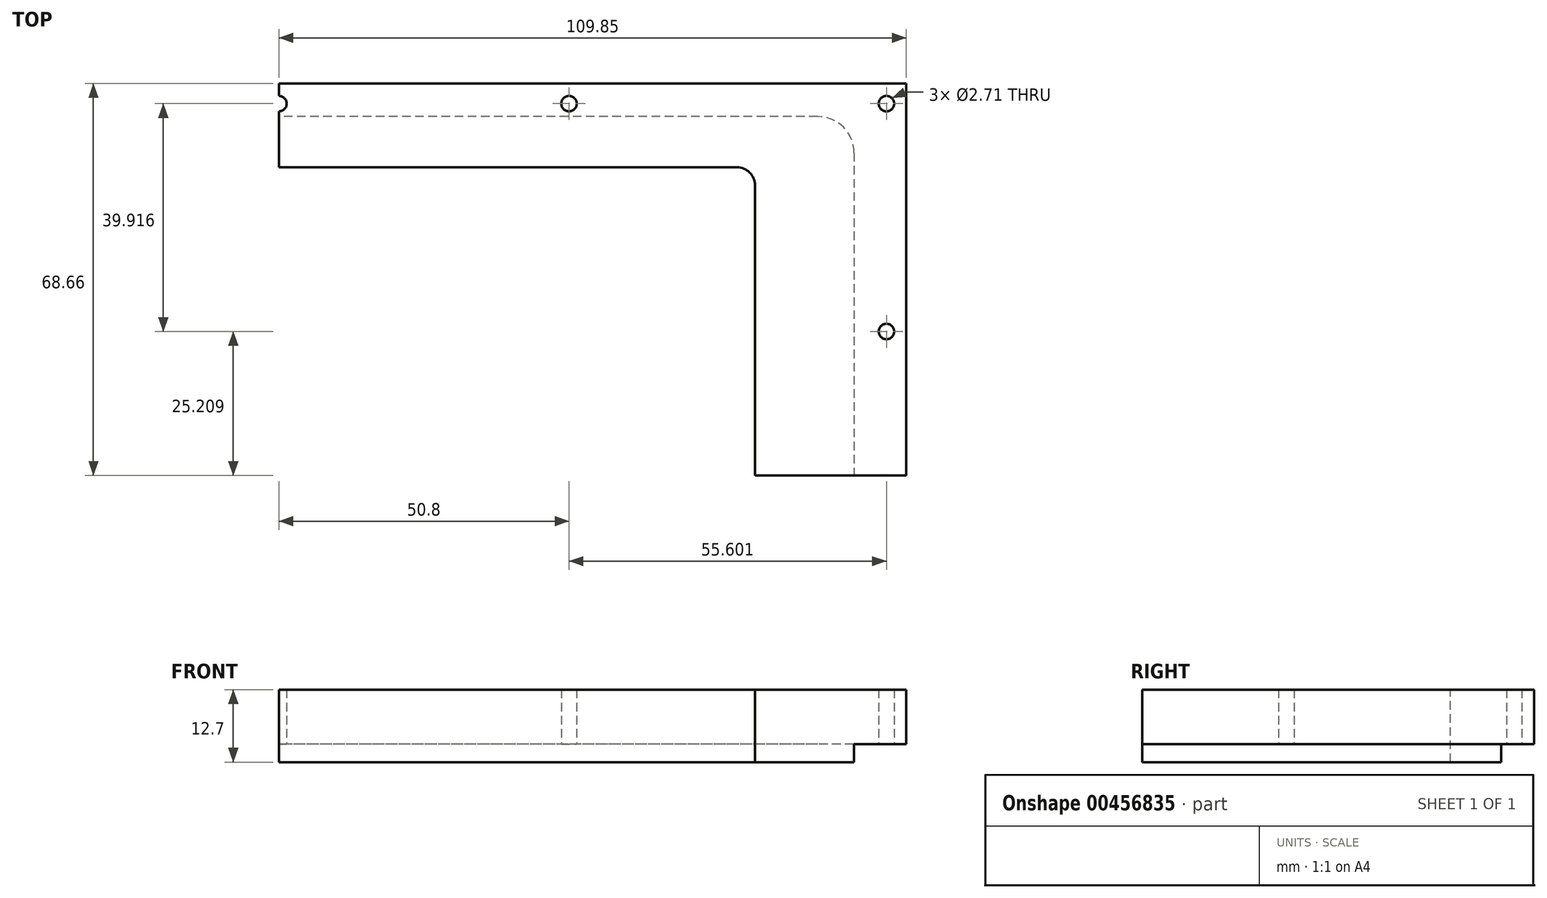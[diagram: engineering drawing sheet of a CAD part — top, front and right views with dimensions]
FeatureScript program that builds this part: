
annotation { "Feature Type Name" : "Feature", "Feature Type Description" : "" }
export const myFeature = defineFeature(function(context is Context, id is Id, definition is map)
    precondition{}
    {
        {
            var Q0;
            Q0=qCreatedBy(makeId("Top.planeOp"),FACE);
            var sketch = newSketch(context, id + "F0", { "sketchPlane" : qUnion([Q0])});
            skLineSegment(sketch, "E0.bottom", {"start": v(94.37, 62.86) * mm, "end": v(-94.37, 62.86) * mm});
            skLineSegment(sketch, "E0.top", {"start": v(94.37, -62.87) * mm, "end": v(-94.37, -62.87) * mm});
            skLineSegment(sketch, "E0.left", {"start": v(100.72, 56.51) * mm, "end": v(100.72, -56.52) * mm});
            skLineSegment(sketch, "E0.right", {"start": v(-100.72, 56.51) * mm, "end": v(-100.72, -56.52) * mm});
            skPoint(sketch, "E0.middle", {"position": v(0, 0) * mm});
            skPoint(sketch, "E1.visualSharp", {"position": v(-100.72, 62.86) * mm});
            skArc(sketch, "E1.filletArc", {"start": v(-94.37, 62.86) * mm, "mid": v(-98.86, 61) * mm, "end": v(-100.72, 56.51) * mm});
            skPoint(sketch, "E2.visualSharp", {"position": v(100.72, 62.86) * mm});
            skArc(sketch, "E2.filletArc", {"start": v(100.72, 56.51) * mm, "mid": v(98.86, 61) * mm, "end": v(94.37, 62.86) * mm});
            skPoint(sketch, "E3.visualSharp", {"position": v(100.72, -62.87) * mm});
            skArc(sketch, "E3.filletArc", {"start": v(94.37, -62.86) * mm, "mid": v(98.86, -61) * mm, "end": v(100.72, -56.52) * mm});
            skPoint(sketch, "E4.visualSharp", {"position": v(-100.72, -62.87) * mm});
            skArc(sketch, "E4.filletArc", {"start": v(-100.72, -56.52) * mm, "mid": v(-98.86, -61) * mm, "end": v(-94.37, -62.87) * mm});
            skLineSegment(sketch, "E5.bottom", {"start": v(80.2, -57.78) * mm, "end": v(-80.2, -57.79) * mm});
            skLineSegment(sketch, "E5.top", {"start": v(80.2, 53.97) * mm, "end": v(-80.2, 53.97) * mm});
            skLineSegment(sketch, "E5.left", {"start": v(83.38, -54.61) * mm, "end": v(83.38, 50.8) * mm});
            skLineSegment(sketch, "E5.right", {"start": v(-83.38, -54.61) * mm, "end": v(-83.38, 50.8) * mm});
            skPoint(sketch, "E5.middle", {"position": v(0, -1.9) * mm});
            skPoint(sketch, "E6.visualSharp", {"position": v(-83.38, 53.97) * mm});
            skArc(sketch, "E6.filletArc", {"start": v(-80.2, 53.97) * mm, "mid": v(-82.45, 53.05) * mm, "end": v(-83.38, 50.8) * mm});
            skPoint(sketch, "E7.visualSharp", {"position": v(83.38, 53.97) * mm});
            skArc(sketch, "E7.filletArc", {"start": v(83.38, 50.8) * mm, "mid": v(82.45, 53.05) * mm, "end": v(80.2, 53.97) * mm});
            skPoint(sketch, "E8.visualSharp", {"position": v(83.38, -57.79) * mm});
            skArc(sketch, "E8.filletArc", {"start": v(80.2, -57.79) * mm, "mid": v(82.45, -56.86) * mm, "end": v(83.38, -54.61) * mm});
            skPoint(sketch, "E9.visualSharp", {"position": v(-83.38, -57.79) * mm});
            skArc(sketch, "E9.filletArc", {"start": v(-83.38, -54.61) * mm, "mid": v(-82.45, -56.86) * mm, "end": v(-80.2, -57.79) * mm});
            skSolve(sketch);
        }
        {
            var Q0;
            Q0 = qSketchRegion(id + "F0", true);
            extrude(context, id + "F1", {"entities" : qUnion([Q0]), "oppositeDirection" : true, "depth" : 3.17 * mm});
        }
        {
            var Q0;
            Q0=makeQuery(id+"F1.opExtrude","CAP_FACE",FACE,{"disambiguationData":[OSD([sQuery(id+"F0.wireOp",EDGE,"E0.bottom"),sQuery(id+"F0.wireOp",EDGE,"E0.top"),sQuery(id+"F0.wireOp",EDGE,"E0.left"),sQuery(id+"F0.wireOp",EDGE,"E0.right"),sQuery(id+"F0.wireOp",EDGE,"E1.filletArc"),sQuery(id+"F0.wireOp",EDGE,"E2.filletArc"),sQuery(id+"F0.wireOp",EDGE,"E3.filletArc"),sQuery(id+"F0.wireOp",EDGE,"E4.filletArc"),sQuery(id+"F0.wireOp",EDGE,"E5.bottom"),sQuery(id+"F0.wireOp",EDGE,"E5.top"),sQuery(id+"F0.wireOp",EDGE,"E5.left"),sQuery(id+"F0.wireOp",EDGE,"E5.right")])],"isStart":true});
            var sketch = newSketch(context, id + "F2", { "sketchPlane" : qUnion([Q0])});
            skLineSegment(sketch, "E10.bottom", {"start": v(109.86, 68.66) * mm, "end": v(-109.86, 68.66) * mm});
            skLineSegment(sketch, "E10.top", {"start": v(109.86, -68.66) * mm, "end": v(-109.86, -68.66) * mm});
            skLineSegment(sketch, "E10.left", {"start": v(109.86, 68.66) * mm, "end": v(109.86, -68.66) * mm});
            skLineSegment(sketch, "E10.right", {"start": v(-109.86, 68.66) * mm, "end": v(-109.86, -68.66) * mm});
            skPoint(sketch, "E10.middle", {"position": v(0, 0) * mm});
            skLineSegment(sketch, "E11.0", {"start": v(80.2, 53.97) * mm, "end": v(-80.2, 53.97) * mm});
            skArc(sketch, "E12.0", {"start": v(-80.2, 53.97) * mm, "mid": v(-82.45, 53.05) * mm, "end": v(-83.38, 50.8) * mm});
            skLineSegment(sketch, "E13.0", {"start": v(-83.38, -54.61) * mm, "end": v(-83.38, 50.8) * mm});
            skArc(sketch, "E14.0", {"start": v(-83.38, -54.61) * mm, "mid": v(-82.45, -56.86) * mm, "end": v(-80.2, -57.79) * mm});
            skLineSegment(sketch, "E15.0", {"start": v(80.2, -57.78) * mm, "end": v(-80.2, -57.79) * mm});
            skArc(sketch, "E16.0", {"start": v(80.2, -57.79) * mm, "mid": v(82.45, -56.86) * mm, "end": v(83.38, -54.61) * mm});
            skLineSegment(sketch, "E17.0", {"start": v(83.38, -54.61) * mm, "end": v(83.38, 50.8) * mm});
            skArc(sketch, "E18.0", {"start": v(83.38, 50.8) * mm, "mid": v(82.45, 53.05) * mm, "end": v(80.2, 53.97) * mm});
            skSolve(sketch);
        }
        {
            var Q0;
            Q0 = qSketchRegion(id + "F2", true);
            extrude(context, id + "F3", {"entities" : qUnion([Q0]), "operationType" : NewBodyOperationType.ADD, "depth" : 9.52 * mm});
        }
        {
            var Q0;
            Q0=makeQuery(id+"F3.opExtrude","CAP_FACE",FACE,{"disambiguationData":[OSD([sQuery(id+"F2.wireOp",EDGE,"E10.bottom"),sQuery(id+"F2.wireOp",EDGE,"E10.top"),sQuery(id+"F2.wireOp",EDGE,"E10.left"),sQuery(id+"F2.wireOp",EDGE,"E10.right"),sQuery(id+"F2.wireOp",EDGE,"E11.0"),sQuery(id+"F2.wireOp",EDGE,"E12.0"),sQuery(id+"F2.wireOp",EDGE,"E13.0"),sQuery(id+"F2.wireOp",EDGE,"E14.0"),sQuery(id+"F2.wireOp",EDGE,"E15.0"),sQuery(id+"F2.wireOp",EDGE,"E16.0"),sQuery(id+"F2.wireOp",EDGE,"E17.0"),sQuery(id+"F2.wireOp",EDGE,"E18.0")])],"isStart":true});
            var sketch = newSketch(context, id + "F4", { "sketchPlane" : qUnion([Q0])});
            skLineSegment(sketch, "E19.bottom", {"start": v(-106.4, -65.13) * mm, "end": v(106.4, -65.13) * mm});
            skLineSegment(sketch, "E19.top", {"start": v(-106.4, 65.13) * mm, "end": v(106.4, 65.13) * mm});
            skLineSegment(sketch, "E19.left", {"start": v(-106.4, -65.13) * mm, "end": v(-106.4, 65.13) * mm});
            skLineSegment(sketch, "E19.right", {"start": v(106.4, -65.13) * mm, "end": v(106.4, 65.13) * mm});
            skPoint(sketch, "E19.middle", {"position": v(0, 0) * mm});
            skPoint(sketch, "E20", {"position": v(106.4, -25.2) * mm});
            skPoint(sketch, "E21", {"position": v(106.4, 25.6) * mm});
            skPoint(sketch, "E22", {"position": v(50.8, 65.13) * mm});
            skPoint(sketch, "E23", {"position": v(0, 65.13) * mm});
            skPoint(sketch, "E24", {"position": v(-50.8, 65.13) * mm});
            skPoint(sketch, "E25", {"position": v(-106.4, 25.6) * mm});
            skPoint(sketch, "E26", {"position": v(-106.4, -25.2) * mm});
            skPoint(sketch, "E27", {"position": v(0, -65.13) * mm});
            skPoint(sketch, "E28", {"position": v(-50.8, -65.13) * mm});
            skPoint(sketch, "E29", {"position": v(50.8, -65.13) * mm});
            skSolve(sketch);
        }
        {
            var Q0;
            Q0=sQuery(id+"F4.wireOp",VERTEX,"E19.right.start");
            var Q1;
            Q1=sQuery(id+"F4.wireOp",VERTEX,"E29");
            var Q2;
            Q2=sQuery(id+"F4.wireOp",VERTEX,"E27");
            var Q3;
            Q3=sQuery(id+"F4.wireOp",VERTEX,"E28");
            var Q4;
            Q4=sQuery(id+"F4.wireOp",VERTEX,"E19.left.start");
            var Q5;
            Q5=sQuery(id+"F4.wireOp",VERTEX,"E26");
            var Q6;
            Q6=sQuery(id+"F4.wireOp",VERTEX,"E25");
            var Q7;
            Q7=sQuery(id+"F4.wireOp",VERTEX,"E19.left.end");
            var Q8;
            Q8=sQuery(id+"F4.wireOp",VERTEX,"E23");
            var Q9;
            Q9=sQuery(id+"F4.wireOp",VERTEX,"E24");
            var Q10;
            Q10=sQuery(id+"F4.wireOp",VERTEX,"E22");
            var Q11;
            Q11=sQuery(id+"F4.wireOp",VERTEX,"E19.top.end");
            var Q12;
            Q12=sQuery(id+"F4.wireOp",VERTEX,"E21");
            var Q13;
            Q13=sQuery(id+"F4.wireOp",VERTEX,"E20");
            var Q14;
            Q14=makeQuery(id+"F1.opExtrude","SWEPT_BODY",BODY,{"disambiguationData":[OSD([sQuery(id+"F0.wireOp",EDGE,"E0.bottom"),sQuery(id+"F0.wireOp",EDGE,"E0.top"),sQuery(id+"F0.wireOp",EDGE,"E0.left"),sQuery(id+"F0.wireOp",EDGE,"E0.right"),sQuery(id+"F0.wireOp",EDGE,"E1.filletArc"),sQuery(id+"F0.wireOp",EDGE,"E2.filletArc"),sQuery(id+"F0.wireOp",EDGE,"E3.filletArc"),sQuery(id+"F0.wireOp",EDGE,"E4.filletArc"),sQuery(id+"F0.wireOp",EDGE,"E5.bottom"),sQuery(id+"F0.wireOp",EDGE,"E5.top"),sQuery(id+"F0.wireOp",EDGE,"E5.left"),sQuery(id+"F0.wireOp",EDGE,"E5.right"),sQuery(id+"F0.wireOp",EDGE,"E6.filletArc"),sQuery(id+"F0.wireOp",EDGE,"E7.filletArc"),sQuery(id+"F0.wireOp",EDGE,"E8.filletArc"),sQuery(id+"F0.wireOp",EDGE,"E9.filletArc")])]});
            hole(context, id + "F5", {"style" : HoleStyle.SIMPLE, "endStyle" : HoleEndStyle.THROUGH, "standardTappedOrClearance" : lookupTablePath({ "standard" : "ANSI", "engagement" : "75%", "pitch" : "32 tpi", "size" : "#6", "type" : "Tapped" }), "standardBlindInLast" : lookupTablePath({ "standard" : "ANSI", "engagement" : "75%", "pitch" : "32 tpi", "size" : "#6", "type" : "Tapped" }), "holeDiameter" : 2.7 * mm, "showTappedDepth" : true, "isTappedThrough" : true, "tappedDepth" : 12.7 * mm, "tapClearance" : 3, "locations" : qUnion([Q0, Q1, Q2, Q3, Q4, Q5, Q6, Q7, Q8, Q9, Q10, Q11, Q12, Q13]), "scope" : qUnion([Q14]), "majorDiameter" : 3.5 * mm});
        }
        {
            var Q0;
            Q0=makeQuery(id+"F3.opExtrude","CAP_FACE",FACE,{"disambiguationData":[OSD([sQuery(id+"F2.wireOp",EDGE,"E10.bottom"),sQuery(id+"F2.wireOp",EDGE,"E10.top"),sQuery(id+"F2.wireOp",EDGE,"E10.left"),sQuery(id+"F2.wireOp",EDGE,"E10.right"),sQuery(id+"F2.wireOp",EDGE,"E11.0"),sQuery(id+"F2.wireOp",EDGE,"E12.0"),sQuery(id+"F2.wireOp",EDGE,"E13.0"),sQuery(id+"F2.wireOp",EDGE,"E14.0"),sQuery(id+"F2.wireOp",EDGE,"E15.0"),sQuery(id+"F2.wireOp",EDGE,"E16.0"),sQuery(id+"F2.wireOp",EDGE,"E17.0"),sQuery(id+"F2.wireOp",EDGE,"E18.0")])],"isStart":true});
            var sketch = newSketch(context, id + "F6", { "sketchPlane" : qUnion([Q0])});
            skLineSegment(sketch, "E30", {"start": v(109.86, 0) * mm, "end": v(0, 0) * mm});
            skLineSegment(sketch, "E31", {"start": v(0, 0) * mm, "end": v(0, -68.66) * mm});
            skPoint(sketch, "E32.orphan", {"position": v(-109.86, -68.66) * mm});
            skPoint(sketch, "E33.orphan", {"position": v(109.86, 68.66) * mm});
            skLineSegment(sketch, "E34", {"start": v(0, -68.66) * mm, "end": v(-109.86, -68.66) * mm});
            skLineSegment(sketch, "E35", {"start": v(-109.86, 68.66) * mm, "end": v(109.86, 68.66) * mm});
            skLineSegment(sketch, "E36", {"start": v(109.86, 0) * mm, "end": v(109.86, 68.66) * mm});
            skLineSegment(sketch, "E37", {"start": v(-109.86, -68.66) * mm, "end": v(-109.86, 68.66) * mm});
            skSolve(sketch);
        }
        {
            var Q0;
            Q0 = qSketchRegion(id + "F6", true);
            extrude(context, id + "F7", {"entities" : qUnion([Q0]), "operationType" : NewBodyOperationType.REMOVE, "endBound" : BoundingType.SYMMETRIC, "oppositeDirection" : true, "depth" : 25.4 * mm, "hasSecondDirection" : true, "secondDirectionOppositeDirection" : true, "secondDirectionDepth" : 25.4 * mm});
        }
    });
